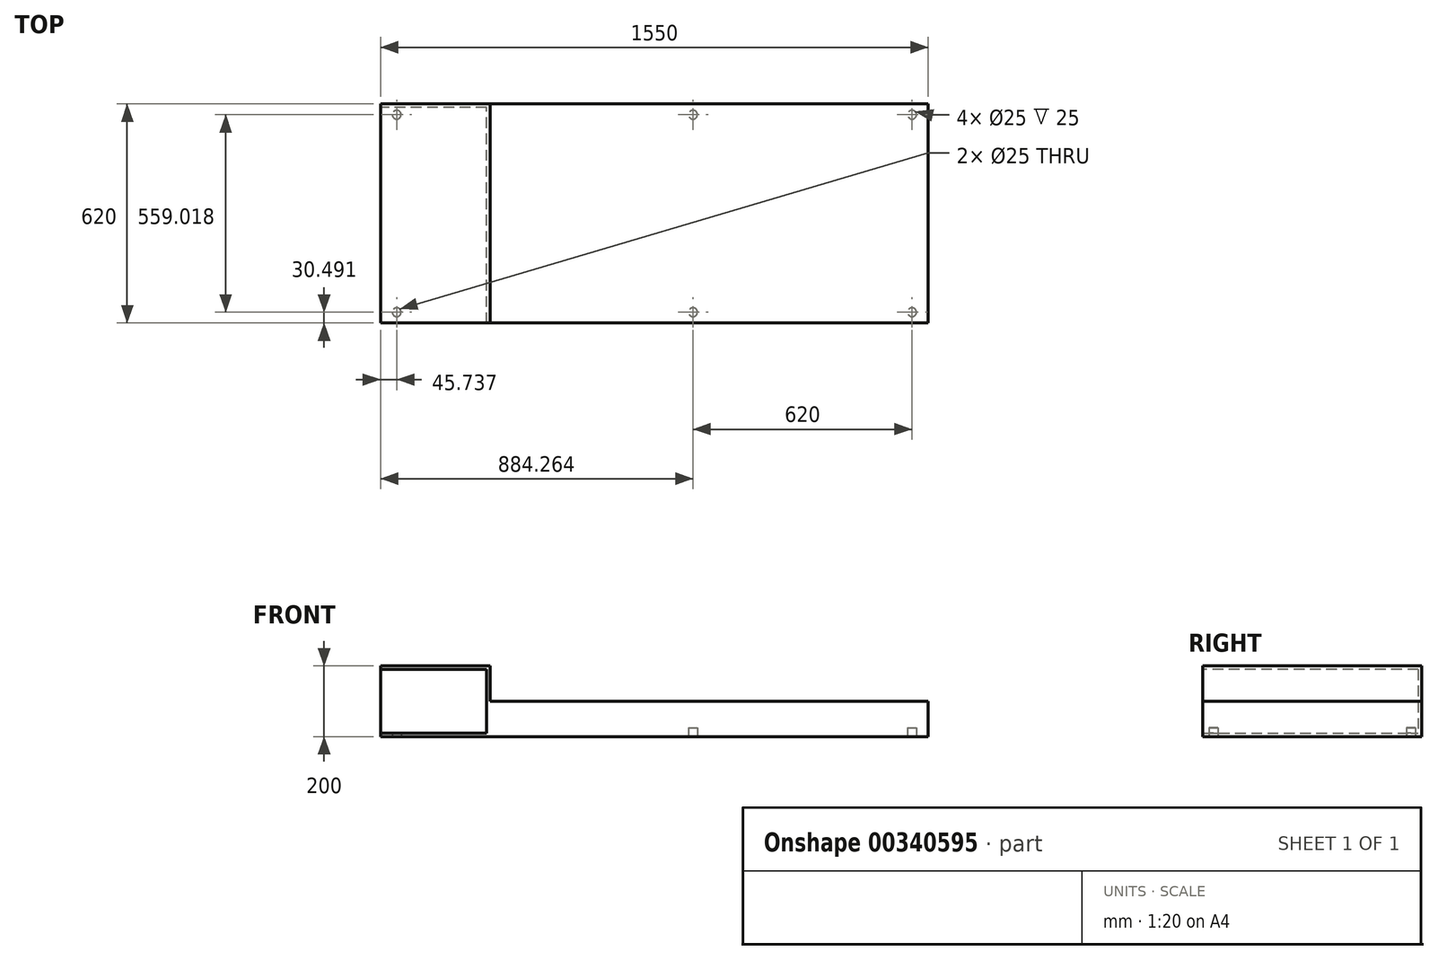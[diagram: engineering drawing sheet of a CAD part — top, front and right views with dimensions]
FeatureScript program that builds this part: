
annotation { "Feature Type Name" : "Feature", "Feature Type Description" : "" }
export const myFeature = defineFeature(function(context is Context, id is Id, definition is map)
    precondition{}
    {
        {
            var Q0;
            Q0=qCreatedBy(makeId("Front.planeOp"),FACE);
            var sketch = newSketch(context, id + "F0", { "sketchPlane" : qUnion([Q0])});
            skLineSegment(sketch, "E0.bottom", {"start": v(266.03, 63.05) * mm, "end": v(-353.97, 63.05) * mm});
            skLineSegment(sketch, "E0.top", {"start": v(266.03, -36.95) * mm, "end": v(-353.97, -36.95) * mm});
            skLineSegment(sketch, "E0.left", {"start": v(266.03, 63.05) * mm, "end": v(266.03, -36.95) * mm});
            skLineSegment(sketch, "E1", {"start": v(-353.97, 63.05) * mm, "end": v(-353.97, 163.05) * mm});
            skLineSegment(sketch, "E2", {"start": v(-353.97, 163.05) * mm, "end": v(-663.97, 163.05) * mm});
            skLineSegment(sketch, "E3", {"start": v(-663.97, 163.05) * mm, "end": v(-663.97, -36.95) * mm});
            skLineSegment(sketch, "E4", {"start": v(-663.97, -36.95) * mm, "end": v(-353.97, -36.95) * mm});
            skSolve(sketch);
        }
        {
            var Q0;
            Q0 = qSketchRegion(id + "F0", true);
            extrude(context, id + "F1", {"entities" : qUnion([Q0]), "depth" : 620 * mm});
        }
        {
            var Q0;
            Q0=makeQuery(id+"F1.opExtrude","SWEPT_FACE",FACE,{"disambiguationData":[OSD([sQuery(id+"F0.wireOp",EDGE,"E0.top"),sQuery(id+"F0.wireOp",EDGE,"E4")])]});
            var sketch = newSketch(context, id + "F2", { "sketchPlane" : qUnion([Q0])});
            skCircle(sketch, "E5", {"center": v(-618.23, 589.5) * mm, "radius": 12.5 * mm});
            skCircle(sketch, "E6", {"center": v(-618.23, 30.5) * mm, "radius": 12.5 * mm});
            skCircle(sketch, "E7", {"center": v(220.3, 589.5) * mm, "radius": 12.5 * mm});
            skCircle(sketch, "E8", {"center": v(220.3, 30.5) * mm, "radius": 12.5 * mm});
            skSolve(sketch);
        }
        {
            var Q0;
            Q0 = qSketchRegion(id + "F2", true);
            extrude(context, id + "F3", {"entities" : qUnion([Q0]), "operationType" : NewBodyOperationType.REMOVE, "oppositeDirection" : true, "depth" : 25 * mm});
        }
        {
            var Q0;
            Q0=makeQuery(id+"F1.opExtrude","SWEPT_FACE",FACE,{"disambiguationData":[OSD([sQuery(id+"F0.wireOp",EDGE,"E3")])]});
            var sketch = newSketch(context, id + "F4", { "sketchPlane" : qUnion([Q0])});
            skLineSegment(sketch, "E9.1", {"start": v(610, 153.05) * mm, "end": v(10, 153.05) * mm});
            skLineSegment(sketch, "E9.3", {"start": v(10, -26.95) * mm, "end": v(610, -26.95) * mm});
            skLineSegment(sketch, "E10", {"start": v(10, 153.05) * mm, "end": v(10, -26.95) * mm});
            skLineSegment(sketch, "E11", {"start": v(610, 153.05) * mm, "end": v(634.78, 153.05) * mm});
            skLineSegment(sketch, "E12", {"start": v(634.78, 153.05) * mm, "end": v(634.78, -26.95) * mm});
            skLineSegment(sketch, "E13", {"start": v(634.78, -26.95) * mm, "end": v(610, -26.95) * mm});
            skSolve(sketch);
        }
        {
            var Q0;
            Q0 = qSketchRegion(id + "F4", true);
            extrude(context, id + "F5", {"entities" : qUnion([Q0]), "operationType" : NewBodyOperationType.REMOVE, "oppositeDirection" : true, "depth" : 300 * mm});
        }
        {
            var Q0;
            Q0=makeQuery(id+"F1.opExtrude","CAP_FACE",FACE,{"disambiguationData":[OSD([sQuery(id+"F0.wireOp",EDGE,"E0.bottom"),sQuery(id+"F0.wireOp",EDGE,"E0.top"),sQuery(id+"F0.wireOp",EDGE,"E0.left"),sQuery(id+"F0.wireOp",EDGE,"E1"),sQuery(id+"F0.wireOp",EDGE,"E2"),sQuery(id+"F0.wireOp",EDGE,"E3"),sQuery(id+"F0.wireOp",EDGE,"E4")])],"isStart":true});
            var sketch = newSketch(context, id + "F6", { "sketchPlane" : qUnion([Q0])});
            skLineSegment(sketch, "E14.bottom", {"start": v(-266.03, 63.05) * mm, "end": v(-886.03, 63.05) * mm});
            skLineSegment(sketch, "E14.top", {"start": v(-266.03, -36.95) * mm, "end": v(-886.03, -36.95) * mm});
            skLineSegment(sketch, "E14.left", {"start": v(-266.03, 63.05) * mm, "end": v(-266.03, -36.95) * mm});
            skLineSegment(sketch, "E14.right", {"start": v(-886.03, 63.05) * mm, "end": v(-886.03, -36.95) * mm});
            skSolve(sketch);
        }
        {
            var Q0;
            Q0 = qSketchRegion(id + "F6", true);
            var Q1;
            Q1=makeQuery(id+"F1.opExtrude","CAP_FACE",FACE,{"disambiguationData":[OSD([sQuery(id+"F0.wireOp",EDGE,"E0.bottom"),sQuery(id+"F0.wireOp",EDGE,"E0.top"),sQuery(id+"F0.wireOp",EDGE,"E0.left"),sQuery(id+"F0.wireOp",EDGE,"E1"),sQuery(id+"F0.wireOp",EDGE,"E2"),sQuery(id+"F0.wireOp",EDGE,"E3"),sQuery(id+"F0.wireOp",EDGE,"E4")])],"isStart":false});
            extrude(context, id + "F7", {"entities" : qUnion([Q0]), "operationType" : NewBodyOperationType.ADD, "endBound" : BoundingType.UP_TO_SURFACE, "oppositeDirection" : true, "endBoundEntityFace" : qUnion([Q1]), "depth" : 25 * mm});
        }
        {
            var Q0;
            Q0=makeQuery(id+"F7.boolean.opBoolean","MERGE",FACE,{"derivedFrom":[makeQuery(id+"F1.opExtrude","SWEPT_FACE",FACE,{"disambiguationData":[OSD([sQuery(id+"F0.wireOp",EDGE,"E0.top"),sQuery(id+"F0.wireOp",EDGE,"E4")])]}),makeQuery(id+"F7.opExtrude","SWEPT_FACE",FACE,{"disambiguationData":[OSD([sQuery(id+"F6.wireOp",EDGE,"E14.top")])]})]});
            var sketch = newSketch(context, id + "F8", { "sketchPlane" : qUnion([Q0])});
            skCircle(sketch, "E15.MirrorC", {"center": v(840.3, 589.5) * mm, "radius": 12.5 * mm});
            skCircle(sketch, "E16.MirrorC", {"center": v(840.3, 30.5) * mm, "radius": 12.5 * mm});
            skPoint(sketch, "E17.start.orphan", {"position": v(111.03, 310) * mm});
            skPoint(sketch, "E18.orphan", {"position": v(886.03, 310) * mm});
            skPoint(sketch, "E19.start.orphan", {"position": v(-663.97, 310) * mm});
            skSolve(sketch);
        }
        {
            var Q0;
            Q0 = qSketchRegion(id + "F8", true);
            var Q1;
            Q1=makeQuery(id+"F3.boolean.opBoolean","COPY",FACE,{"derivedFrom":makeQuery(id+"F3.opExtrude","CAP_FACE",FACE,{"disambiguationData":[OSD([sQuery(id+"F2.wireOp",EDGE,"E7")])],"isStart":false})});
            extrude(context, id + "F9", {"entities" : qUnion([Q0]), "operationType" : NewBodyOperationType.REMOVE, "endBound" : BoundingType.UP_TO_SURFACE, "oppositeDirection" : true, "endBoundEntityFace" : qUnion([Q1]), "depth" : 25 * mm});
        }
    });
